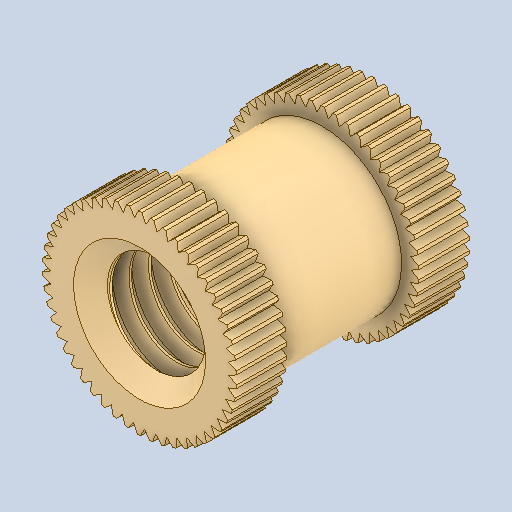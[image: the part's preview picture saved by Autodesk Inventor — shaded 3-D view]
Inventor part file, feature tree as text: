
AUTODESK INVENTOR PART (.ipt)
format: ipt  version: 2022 (Build 260153000, 153)  size: 1,609,216 bytes
history: mixed  units: in
note: dims shown in document units (in); Inventor stores cm internally (conversion verified against a paired STEP export)
features: thread x1, imported_body x1
ambient origin geometry x8: Origin, YZ Plane, XZ Plane, XY Plane, X Axis, Y Axis, Z Axis, Center Point
bodies: Solid1 (imported_parasolid)
feature tree (2):
  thread  "Thread Insert M3 x 6mm v2.step"  [1 undecoded]
  imported_body  NMx_Import_Brep_tag  [imported B-rep: ~5 faces, bbox_mm=None]
note: 1 required parameter value undecoded (feature->parameter linkage not recoverable at this tier; creation-order binding heuristic only, values carry confidence <= 0.55)
